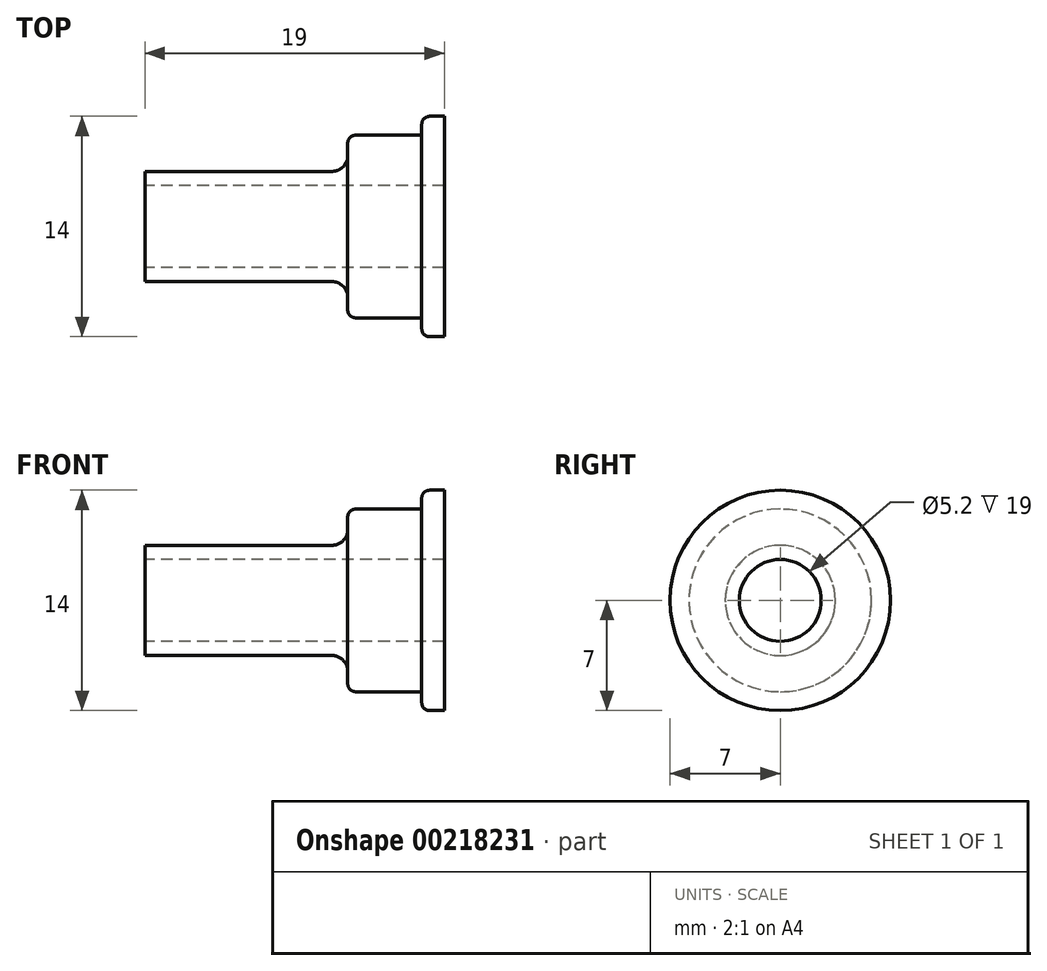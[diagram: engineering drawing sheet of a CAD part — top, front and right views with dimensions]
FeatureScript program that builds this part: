
annotation { "Feature Type Name" : "Feature", "Feature Type Description" : "" }
export const myFeature = defineFeature(function(context is Context, id is Id, definition is map)
    precondition{}
    {
        {
            var Q0;
            Q0=qCreatedBy(makeId("Top.planeOp"),FACE);
            var sketch = newSketch(context, id + "F0", { "sketchPlane" : qUnion([Q0])});
            skLineSegment(sketch, "E0", {"start": v(0, 3.5) * mm, "end": v(12.87, 3.5) * mm});
            skLineSegment(sketch, "E1", {"start": v(19, 7) * mm, "end": v(19, 2.6) * mm});
            skLineSegment(sketch, "E2", {"start": v(19, 2.6) * mm, "end": v(17.44, 2.6) * mm});
            skLineSegment(sketch, "E3", {"start": v(0, 2.6) * mm, "end": v(0, 3.5) * mm});
            skLineSegment(sketch, "E4", {"start": v(-2.93, 0) * mm, "end": v(20.9, 0) * mm, "construction": true});
            skLineSegment(sketch, "E5", {"start": v(0, 2.6) * mm, "end": v(1.56, 2.6) * mm});
            skLineSegment(sketch, "E6", {"start": v(1.56, 2.6) * mm, "end": v(0, 2.6) * mm});
            skLineSegment(sketch, "E7", {"start": v(17.57, 5.8) * mm, "end": v(12.87, 5.8) * mm});
            skLineSegment(sketch, "E8", {"start": v(12.87, 5.8) * mm, "end": v(12.87, 3.5) * mm});
            skLineSegment(sketch, "E9", {"start": v(17.57, 7) * mm, "end": v(19, 7) * mm});
            skLineSegment(sketch, "E10", {"start": v(17.57, 5.8) * mm, "end": v(17.57, 7) * mm});
            skLineSegment(sketch, "E11", {"start": v(1.56, 2.6) * mm, "end": v(17.44, 2.6) * mm});
            skSolve(sketch);
        }
        {
            var Q0;
            Q0=makeQuery(id+"F0.imprint","IMPRINT",FACE,{"disambiguationData":[TD([[makeQuery(id+"F0.imprint","IMPRINT",EDGE,{"derivedFrom":sQuery(id+"F0.wireOp",EDGE,"E0")}),-1.0]])]});
            var Q1;
            Q1=sQuery(id+"F0.wireOp",EDGE,"E4");
            revolve(context, id + "F1", {"entities" : qUnion([Q0]), "axis" : qUnion([Q1]), "revolveType" : RevolveType.FULL});
        }
        {
            var Q0;
            Q0=makeQuery(id+"F1.opRevolve","SWEPT_EDGE",EDGE,{"disambiguationData":[OSD([sQuery(id+"F0.wireOp",EDGE,"E0"),sQuery(id+"F0.wireOp",EDGE,"E8")])]});
            fillet(context, id + "F2", {"entities" : qUnion([Q0]), "radius" : 1 * mm, "tangentPropagation" : true, "allowEdgeOverflow" : false});
        }
        {
            var Q0;
            Q0=makeQuery(id+"F1.opRevolve","SWEPT_EDGE",EDGE,{"disambiguationData":[OSD([sQuery(id+"F0.wireOp",EDGE,"E9"),sQuery(id+"F0.wireOp",EDGE,"E10")])]});
            var Q1;
            Q1=makeQuery(id+"F1.opRevolve","SWEPT_EDGE",EDGE,{"disambiguationData":[OSD([sQuery(id+"F0.wireOp",EDGE,"E7"),sQuery(id+"F0.wireOp",EDGE,"E8")])]});
            fillet(context, id + "F3", {"entities" : qUnion([Q0, Q1]), "radius" : .5 * mm, "tangentPropagation" : true, "allowEdgeOverflow" : false});
        }
    });
